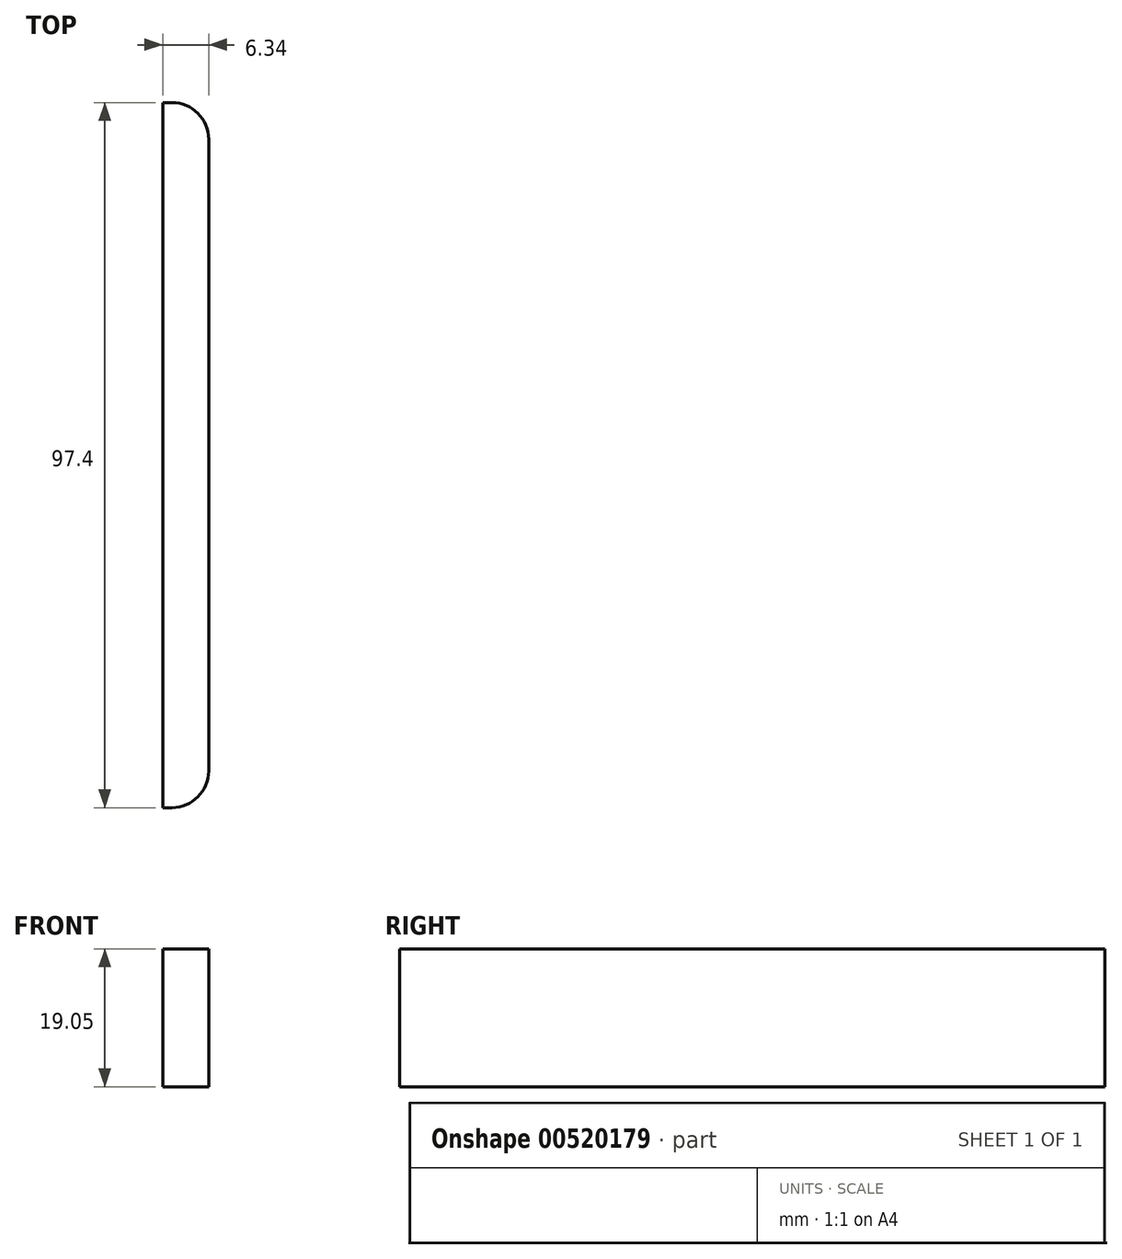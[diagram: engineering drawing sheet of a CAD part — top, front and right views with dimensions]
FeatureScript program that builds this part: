
annotation { "Feature Type Name" : "Feature", "Feature Type Description" : "" }
export const myFeature = defineFeature(function(context is Context, id is Id, definition is map)
    precondition{}
    {
        {
            var Q0;
            Q0=qCreatedBy(makeId("Top.planeOp"),FACE);
            var sketch = newSketch(context, id + "F0", { "sketchPlane" : qUnion([Q0])});
            skLineSegment(sketch, "E0.bottom", {"start": v(-3.17, 48.7) * mm, "end": v(3.18, 48.7) * mm});
            skLineSegment(sketch, "E0.top", {"start": v(-3.18, -48.7) * mm, "end": v(3.17, -48.7) * mm});
            skLineSegment(sketch, "E0.left", {"start": v(-3.17, 48.7) * mm, "end": v(-3.18, -48.7) * mm});
            skLineSegment(sketch, "E0.right", {"start": v(3.18, 48.7) * mm, "end": v(3.17, -48.7) * mm});
            skPoint(sketch, "E0.middle", {"position": v(0, 0) * mm});
            skSolve(sketch);
        }
        {
            var Q0;
            Q0 = qSketchRegion(id + "F0", true);
            extrude(context, id + "F1", {"entities" : qUnion([Q0]), "depth" : 19.05 * mm, "offsetDistance" : 25.4 * mm});
        }
        {
            var Q0;
            Q0=makeQuery(id+"F1.opExtrude","SWEPT_EDGE",EDGE,{"disambiguationData":[OSD([sQuery(id+"F0.wireOp",EDGE,"E0.top"),sQuery(id+"F0.wireOp",EDGE,"E0.right")])]});
            var Q1;
            Q1=makeQuery(id+"F1.opExtrude","SWEPT_EDGE",EDGE,{"disambiguationData":[OSD([sQuery(id+"F0.wireOp",EDGE,"E0.bottom"),sQuery(id+"F0.wireOp",EDGE,"E0.right")])]});
            fillet(context, id + "F2", {"entities" : qUnion([Q0, Q1]), "radius" : 5.08 * mm, "tangentPropagation" : true, "allowEdgeOverflow" : false});
        }
    });
